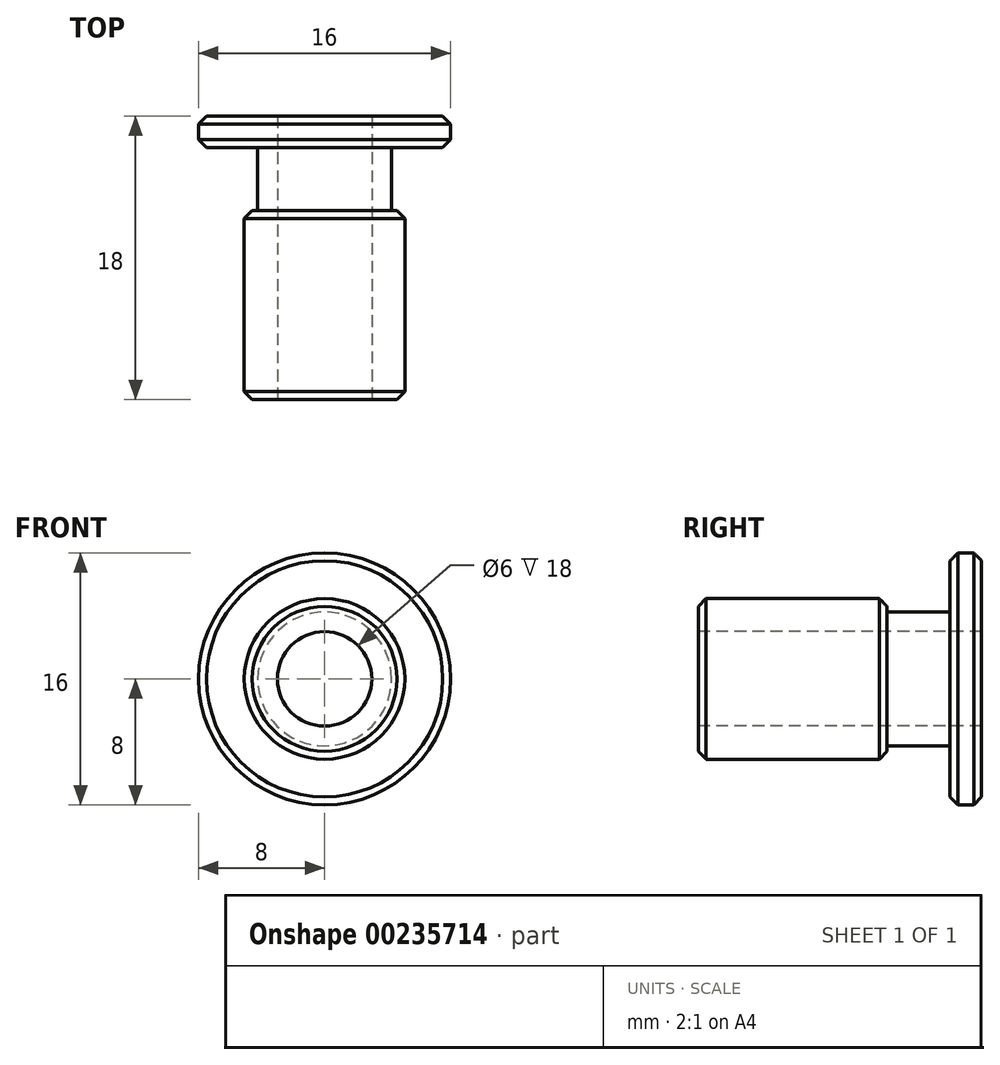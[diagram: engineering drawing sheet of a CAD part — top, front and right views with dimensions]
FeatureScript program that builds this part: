
annotation { "Feature Type Name" : "Feature", "Feature Type Description" : "" }
export const myFeature = defineFeature(function(context is Context, id is Id, definition is map)
    precondition{}
    {
        {
            var Q0;
            Q0=qCreatedBy(makeId("Top.planeOp"),FACE);
            var sketch = newSketch(context, id + "F0", { "sketchPlane" : qUnion([Q0])});
            skLineSegment(sketch, "E0.right", {"start": v(-5.1, 0) * mm, "end": v(-5.1, 12) * mm});
            skLineSegment(sketch, "E1.right", {"start": v(-8, 18) * mm, "end": v(-8, 16) * mm});
            skLineSegment(sketch, "E2", {"start": v(-5.1, 12) * mm, "end": v(-4.25, 12) * mm});
            skLineSegment(sketch, "E3.right", {"start": v(-4.25, 16) * mm, "end": v(-4.25, 12) * mm});
            skLineSegment(sketch, "E4", {"start": v(-8, 16) * mm, "end": v(-4.25, 16) * mm});
            skLineSegment(sketch, "E5", {"start": v(-8, 18) * mm, "end": v(-3, 18) * mm});
            skLineSegment(sketch, "E6.right", {"start": v(-3, 18) * mm, "end": v(-3, 0) * mm});
            skLineSegment(sketch, "E7", {"start": v(-3, 0) * mm, "end": v(-5.1, 0) * mm});
            skLineSegment(sketch, "E8", {"start": v(0, 0) * mm, "end": v(0, 18) * mm, "construction": true});
            skLineSegment(sketch, "E9", {"start": v(0, 0) * mm, "end": v(-9.61, 0) * mm, "construction": true});
            skSolve(sketch);
        }
        {
            var Q0;
            Q0 = qSketchRegion(id + "F0", true);
            var Q1;
            Q1=sQuery(id+"F0.wireOp",EDGE,"E8");
            revolve(context, id + "F1", {"entities" : qUnion([Q0]), "axis" : qUnion([Q1]), "revolveType" : RevolveType.FULL});
        }
        {
            var Q0;
            Q0=makeQuery(id+"F1.opRevolve","SWEPT_EDGE",EDGE,{"disambiguationData":[OSD([sQuery(id+"F0.wireOp",EDGE,"E1.right"),sQuery(id+"F0.wireOp",EDGE,"E5")])]});
            var Q1;
            Q1=makeQuery(id+"F1.opRevolve","SWEPT_FACE",FACE,{"disambiguationData":[OSD([sQuery(id+"F0.wireOp",EDGE,"E1.right")])]});
            var Q2;
            Q2=makeQuery(id+"F1.opRevolve","SWEPT_FACE",FACE,{"disambiguationData":[OSD([sQuery(id+"F0.wireOp",EDGE,"E0.right")])]});
            chamfer(context, id + "F2", {"entities" : qUnion([Q0, Q1, Q2]), "width" : .5 * mm, "tangentPropagation" : true});
        }
    });
